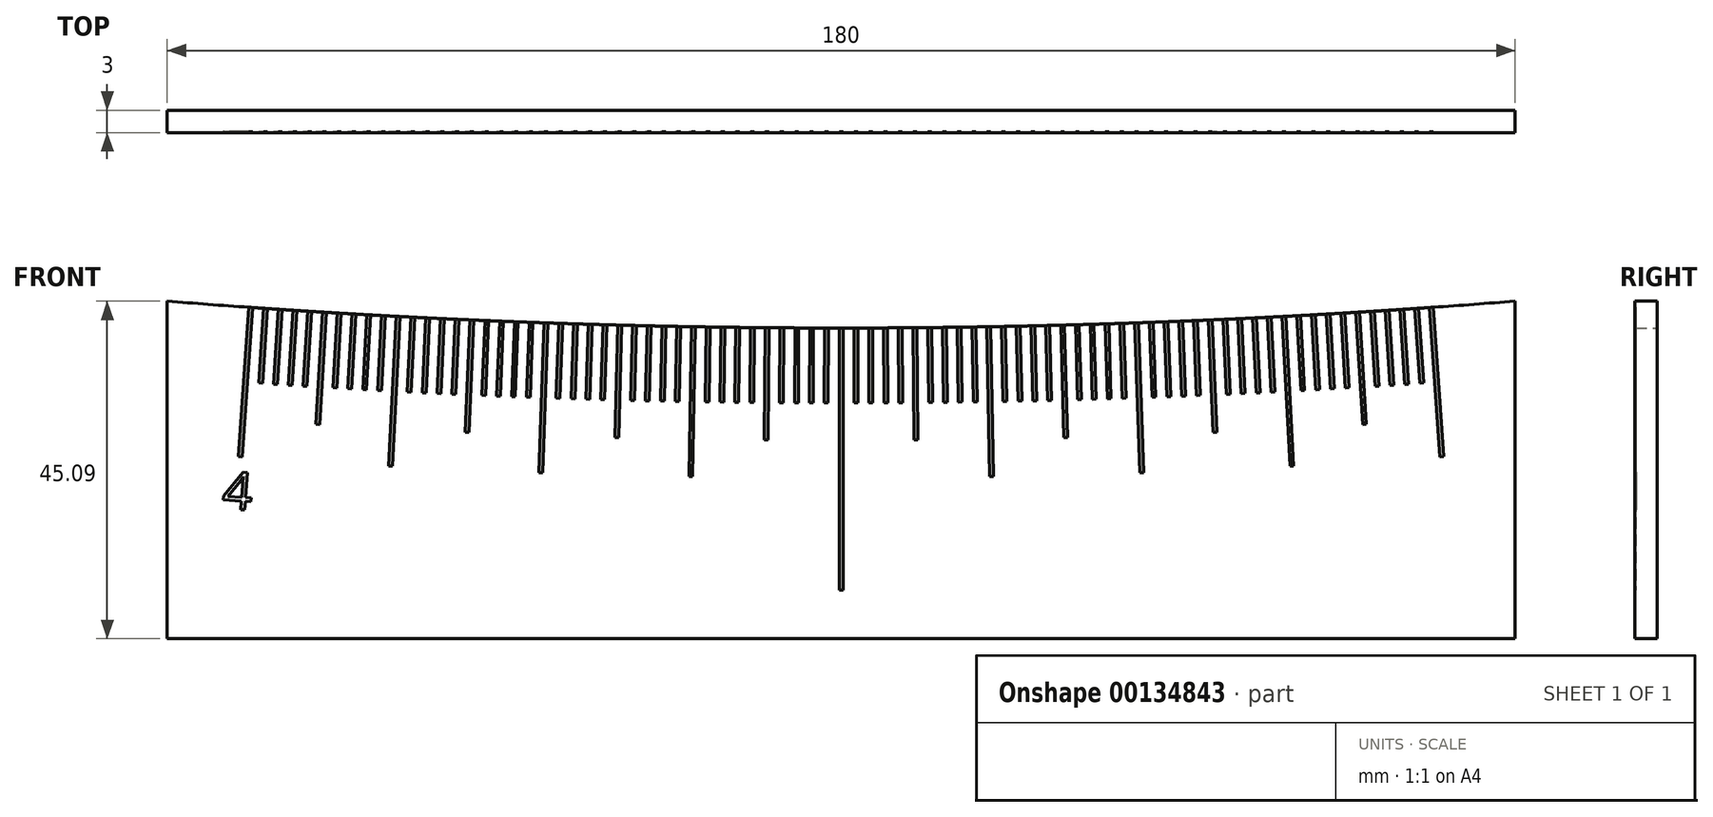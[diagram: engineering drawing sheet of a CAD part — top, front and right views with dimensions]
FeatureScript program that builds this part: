
annotation { "Feature Type Name" : "Feature", "Feature Type Description" : "" }
export const myFeature = defineFeature(function(context is Context, id is Id, definition is map)
    precondition{}
    {
        {
            var Q0;
            Q0=qCreatedBy(makeId("Front.planeOp"),FACE);
            var sketch = newSketch(context, id + "F0", { "sketchPlane" : qUnion([Q0])});
            skCircle(sketch, "E0", {"center": v(0, 1130) * mm, "radius": 1130 * mm});
            skLineSegment(sketch, "E1.rect.bottom", {"start": v(90, -41.5) * mm, "end": v(-90, -41.5) * mm});
            skLineSegment(sketch, "E1.rect.top", {"start": v(90, 41.5) * mm, "end": v(-90, 41.5) * mm});
            skLineSegment(sketch, "E1.rect.left", {"start": v(90, -41.5) * mm, "end": v(90, 41.5) * mm});
            skLineSegment(sketch, "E1.rect.right", {"start": v(-90, -41.5) * mm, "end": v(-90, 41.5) * mm});
            skPoint(sketch, "E1.rect.middle", {"position": v(0, 0) * mm});
            skSolve(sketch);
        }
        {
            var Q0;
            {var subQ3=sQuery(id+"F0.wireOp",EDGE,"E1.rect.bottom");Q0=makeQuery(id+"F0.imprint","IMPRINT",FACE,{"disambiguationData":[TD([[makeQuery(id+"F0.imprint","IMPRINT",EDGE,{"derivedFrom":subQ3}),-1.0]])]});}
            extrude(context, id + "F1", {"entities" : qUnion([Q0]), "depth" : 3 * mm});
        }
        {
            var Q0;
            Q0=makeQuery(id+"F1.opExtrude","CAP_FACE",FACE,{"disambiguationData":[OSD([sQuery(id+"F0.wireOp",EDGE,"E0"),sQuery(id+"F0.wireOp",EDGE,"E1.rect.bottom"),sQuery(id+"F0.wireOp",EDGE,"E1.rect.left"),sQuery(id+"F0.wireOp",EDGE,"E1.rect.right")])],"isStart":false});
            var sketch = newSketch(context, id + "F2", { "sketchPlane" : qUnion([Q0])});
            skLineSegment(sketch, "E2.rect.bottom", {"start": v(0.25, 20) * mm, "end": v(-0.25, 20) * mm});
            skLineSegment(sketch, "E2.rect.top", {"start": v(0.25, -20) * mm, "end": v(-0.25, -20) * mm});
            skLineSegment(sketch, "E2.rect.left", {"start": v(0.25, 20) * mm, "end": v(0.25, -20) * mm});
            skLineSegment(sketch, "E2.rect.right", {"start": v(-0.25, 20) * mm, "end": v(-0.25, -20) * mm});
            skPoint(sketch, "E2.rect.middle", {"position": v(0, 0) * mm});
            skLineSegment(sketch, "E3.1.0", {"start": v(-19.12, 20.16) * mm, "end": v(-19.62, 20.17) * mm});
            skLineSegment(sketch, "E3.1.1", {"start": v(-19.62, 20.17) * mm, "end": v(-20.32, -19.82) * mm});
            skLineSegment(sketch, "E3.1.2", {"start": v(-19.12, 20.16) * mm, "end": v(-19.82, -19.83) * mm});
            skLineSegment(sketch, "E3.1.3", {"start": v(-19.82, -19.83) * mm, "end": v(-20.32, -19.82) * mm});
            skLineSegment(sketch, "E3.2.0", {"start": v(-38.49, 20.67) * mm, "end": v(-38.99, 20.68) * mm});
            skLineSegment(sketch, "E3.2.1", {"start": v(-38.99, 20.68) * mm, "end": v(-40.38, -19.3) * mm});
            skLineSegment(sketch, "E3.2.2", {"start": v(-38.49, 20.67) * mm, "end": v(-39.88, -19.3) * mm});
            skLineSegment(sketch, "E3.2.3", {"start": v(-39.88, -19.3) * mm, "end": v(-40.38, -19.3) * mm});
            skLineSegment(sketch, "E3.3.0", {"start": v(-57.84, 21.5) * mm, "end": v(-58.34, 21.53) * mm});
            skLineSegment(sketch, "E3.3.1", {"start": v(-58.34, 21.53) * mm, "end": v(-60.44, -18.41) * mm});
            skLineSegment(sketch, "E3.3.2", {"start": v(-57.84, 21.5) * mm, "end": v(-59.94, -18.44) * mm});
            skLineSegment(sketch, "E3.3.3", {"start": v(-59.94, -18.44) * mm, "end": v(-60.44, -18.41) * mm});
            skLineSegment(sketch, "E3.4.0", {"start": v(-77.18, 22.69) * mm, "end": v(-77.68, 22.72) * mm});
            skLineSegment(sketch, "E3.4.1", {"start": v(-77.68, 22.72) * mm, "end": v(-80.47, -17.18) * mm});
            skLineSegment(sketch, "E3.4.2", {"start": v(-77.18, 22.69) * mm, "end": v(-79.97, -17.22) * mm});
            skLineSegment(sketch, "E3.4.3", {"start": v(-79.97, -17.22) * mm, "end": v(-80.47, -17.18) * mm});
            skPoint(sketch, "E3.center", {"position": v(0, 1130) * mm});
            skLineSegment(sketch, "E3.anchor1", {"start": v(0, 1130) * mm, "end": v(-0.25, 20) * mm, "construction": true});
            skLineSegment(sketch, "E3.anchor2", {"start": v(0, 1130) * mm, "end": v(-77.68, 22.72) * mm, "construction": true});
            skSolve(sketch);
        }
        {
            var Q0;
            Q0=qSketchRegion(id+"F2",true);
            extrude(context, id + "F3", {"entities" : qUnion([Q0]), "operationType" : NewBodyOperationType.REMOVE, "oppositeDirection" : true, "depth" : 0.1 * mm});
        }
        {
            var Q0;
            Q0=makeQuery(id+"F1.opExtrude","SWEPT_BODY",BODY,{"disambiguationData":[OSD([sQuery(id+"F0.wireOp",EDGE,"E0"),sQuery(id+"F0.wireOp",EDGE,"E1.rect.bottom"),sQuery(id+"F0.wireOp",EDGE,"E1.rect.left"),sQuery(id+"F0.wireOp",EDGE,"E1.rect.right")])]});
            var Q1;
            Q1=qCreatedBy(makeId("Right.planeOp"),FACE);
            mirror(context, id + "F4", {"operationType" : NewBodyOperationType.INTERSECT, "entities" : qUnion([Q0]), "mirrorPlane" : qUnion([Q1])});
        }
        {
            var Q0;
            Q0=makeQuery(id+"F1.opExtrude","CAP_FACE",FACE,{"disambiguationData":[OSD([sQuery(id+"F0.wireOp",EDGE,"E0"),sQuery(id+"F0.wireOp",EDGE,"E1.rect.bottom"),sQuery(id+"F0.wireOp",EDGE,"E1.rect.left"),sQuery(id+"F0.wireOp",EDGE,"E1.rect.right")])],"isStart":false});
            var sketch = newSketch(context, id + "F5", { "sketchPlane" : qUnion([Q0])});
            skLineSegment(sketch, "E4.rect.bottom", {"start": v(0.25, 10) * mm, "end": v(-0.25, 10) * mm});
            skLineSegment(sketch, "E4.rect.top", {"start": v(0.25, -10) * mm, "end": v(-0.25, -10) * mm});
            skLineSegment(sketch, "E4.rect.left", {"start": v(0.25, 10) * mm, "end": v(0.25, -10) * mm});
            skLineSegment(sketch, "E4.rect.right", {"start": v(-0.25, 10) * mm, "end": v(-0.25, -10) * mm});
            skPoint(sketch, "E4.rect.middle", {"position": v(0, 0) * mm});
            skLineSegment(sketch, "E5.1.0", {"start": v(-1.74, -10) * mm, "end": v(-2.24, -10) * mm});
            skLineSegment(sketch, "E5.1.1", {"start": v(-1.7, 10) * mm, "end": v(-1.74, -10) * mm});
            skLineSegment(sketch, "E5.1.2", {"start": v(-2.2, 10) * mm, "end": v(-2.24, -10) * mm});
            skLineSegment(sketch, "E5.1.3", {"start": v(-1.7, 10) * mm, "end": v(-2.2, 10) * mm});
            skLineSegment(sketch, "E5.2.0", {"start": v(-3.73, -10) * mm, "end": v(-4.23, -10) * mm});
            skLineSegment(sketch, "E5.2.1", {"start": v(-3.66, 10) * mm, "end": v(-3.73, -10) * mm});
            skLineSegment(sketch, "E5.2.2", {"start": v(-4.16, 10) * mm, "end": v(-4.23, -10) * mm});
            skLineSegment(sketch, "E5.2.3", {"start": v(-3.66, 10) * mm, "end": v(-4.16, 10) * mm});
            skLineSegment(sketch, "E5.3.0", {"start": v(-5.72, -9.99) * mm, "end": v(-6.22, -9.98) * mm});
            skLineSegment(sketch, "E5.3.1", {"start": v(-5.61, 10.01) * mm, "end": v(-5.72, -9.99) * mm});
            skLineSegment(sketch, "E5.3.2", {"start": v(-6.11, 10.02) * mm, "end": v(-6.22, -9.98) * mm});
            skLineSegment(sketch, "E5.3.3", {"start": v(-5.61, 10.01) * mm, "end": v(-6.11, 10.02) * mm});
            skLineSegment(sketch, "E5.4.0", {"start": v(-7.7, -9.97) * mm, "end": v(-8.2, -9.97) * mm});
            skLineSegment(sketch, "E5.4.1", {"start": v(-7.57, 10.03) * mm, "end": v(-7.7, -9.97) * mm});
            skLineSegment(sketch, "E5.4.2", {"start": v(-8.07, 10.03) * mm, "end": v(-8.2, -9.97) * mm});
            skLineSegment(sketch, "E5.4.3", {"start": v(-7.57, 10.03) * mm, "end": v(-8.07, 10.03) * mm});
            skLineSegment(sketch, "E5.5.0", {"start": v(-9.7, -9.96) * mm, "end": v(-10.2, -9.95) * mm});
            skLineSegment(sketch, "E5.5.1", {"start": v(-9.52, 10.04) * mm, "end": v(-9.7, -9.96) * mm});
            skLineSegment(sketch, "E5.5.2", {"start": v(-10.02, 10.04) * mm, "end": v(-10.2, -9.95) * mm});
            skLineSegment(sketch, "E5.5.3", {"start": v(-9.52, 10.04) * mm, "end": v(-10.02, 10.04) * mm});
            skLineSegment(sketch, "E5.6.0", {"start": v(-11.69, -9.94) * mm, "end": v(-12.19, -9.93) * mm});
            skLineSegment(sketch, "E5.6.1", {"start": v(-11.48, 10.06) * mm, "end": v(-11.69, -9.94) * mm});
            skLineSegment(sketch, "E5.6.2", {"start": v(-11.98, 10.06) * mm, "end": v(-12.19, -9.93) * mm});
            skLineSegment(sketch, "E5.6.3", {"start": v(-11.48, 10.06) * mm, "end": v(-11.98, 10.06) * mm});
            skLineSegment(sketch, "E5.7.0", {"start": v(-13.68, -9.92) * mm, "end": v(-14.18, -9.91) * mm});
            skLineSegment(sketch, "E5.7.1", {"start": v(-13.43, 10.08) * mm, "end": v(-13.68, -9.92) * mm});
            skLineSegment(sketch, "E5.7.2", {"start": v(-13.93, 10.09) * mm, "end": v(-14.18, -9.91) * mm});
            skLineSegment(sketch, "E5.7.3", {"start": v(-13.43, 10.08) * mm, "end": v(-13.93, 10.09) * mm});
            skLineSegment(sketch, "E5.8.0", {"start": v(-15.67, -9.9) * mm, "end": v(-16.17, -9.89) * mm});
            skLineSegment(sketch, "E5.8.1", {"start": v(-15.39, 10.1) * mm, "end": v(-15.67, -9.9) * mm});
            skLineSegment(sketch, "E5.8.2", {"start": v(-15.89, 10.11) * mm, "end": v(-16.17, -9.89) * mm});
            skLineSegment(sketch, "E5.8.3", {"start": v(-15.39, 10.1) * mm, "end": v(-15.89, 10.11) * mm});
            skLineSegment(sketch, "E5.9.0", {"start": v(-17.66, -9.86) * mm, "end": v(-18.16, -9.86) * mm});
            skLineSegment(sketch, "E5.9.1", {"start": v(-17.34, 10.13) * mm, "end": v(-17.66, -9.86) * mm});
            skLineSegment(sketch, "E5.9.2", {"start": v(-17.84, 10.14) * mm, "end": v(-18.16, -9.86) * mm});
            skLineSegment(sketch, "E5.9.3", {"start": v(-17.34, 10.13) * mm, "end": v(-17.84, 10.14) * mm});
            skLineSegment(sketch, "E5.10.0", {"start": v(-19.65, -9.83) * mm, "end": v(-20.15, -9.82) * mm});
            skLineSegment(sketch, "E5.10.1", {"start": v(-19.3, 10.17) * mm, "end": v(-19.65, -9.83) * mm});
            skLineSegment(sketch, "E5.10.2", {"start": v(-19.8, 10.17) * mm, "end": v(-20.15, -9.82) * mm});
            skLineSegment(sketch, "E5.10.3", {"start": v(-19.3, 10.17) * mm, "end": v(-19.8, 10.17) * mm});
            skLineSegment(sketch, "E5.11.0", {"start": v(-21.64, -9.8) * mm, "end": v(-22.14, -9.79) * mm});
            skLineSegment(sketch, "E5.11.1", {"start": v(-21.25, 10.2) * mm, "end": v(-21.64, -9.8) * mm});
            skLineSegment(sketch, "E5.11.2", {"start": v(-21.75, 10.21) * mm, "end": v(-22.14, -9.79) * mm});
            skLineSegment(sketch, "E5.11.3", {"start": v(-21.25, 10.2) * mm, "end": v(-21.75, 10.21) * mm});
            skLineSegment(sketch, "E5.12.0", {"start": v(-23.62, -9.76) * mm, "end": v(-24.12, -9.74) * mm});
            skLineSegment(sketch, "E5.12.1", {"start": v(-23.2, 10.24) * mm, "end": v(-23.62, -9.76) * mm});
            skLineSegment(sketch, "E5.12.2", {"start": v(-23.7, 10.25) * mm, "end": v(-24.12, -9.74) * mm});
            skLineSegment(sketch, "E5.12.3", {"start": v(-23.2, 10.24) * mm, "end": v(-23.7, 10.25) * mm});
            skLineSegment(sketch, "E5.13.0", {"start": v(-25.61, -9.71) * mm, "end": v(-26.11, -9.7) * mm});
            skLineSegment(sketch, "E5.13.1", {"start": v(-25.16, 10.28) * mm, "end": v(-25.61, -9.71) * mm});
            skLineSegment(sketch, "E5.13.2", {"start": v(-25.66, 10.3) * mm, "end": v(-26.11, -9.7) * mm});
            skLineSegment(sketch, "E5.13.3", {"start": v(-25.16, 10.28) * mm, "end": v(-25.66, 10.3) * mm});
            skLineSegment(sketch, "E5.14.0", {"start": v(-27.6, -9.67) * mm, "end": v(-28.1, -9.65) * mm});
            skLineSegment(sketch, "E5.14.1", {"start": v(-27.11, 10.33) * mm, "end": v(-27.6, -9.67) * mm});
            skLineSegment(sketch, "E5.14.2", {"start": v(-27.61, 10.34) * mm, "end": v(-28.1, -9.65) * mm});
            skLineSegment(sketch, "E5.14.3", {"start": v(-27.11, 10.33) * mm, "end": v(-27.61, 10.34) * mm});
            skLineSegment(sketch, "E5.15.0", {"start": v(-29.6, -9.62) * mm, "end": v(-30.1, -9.6) * mm});
            skLineSegment(sketch, "E5.15.1", {"start": v(-29.07, 10.38) * mm, "end": v(-29.6, -9.62) * mm});
            skLineSegment(sketch, "E5.15.2", {"start": v(-29.57, 10.4) * mm, "end": v(-30.1, -9.6) * mm});
            skLineSegment(sketch, "E5.15.3", {"start": v(-29.07, 10.38) * mm, "end": v(-29.57, 10.4) * mm});
            skLineSegment(sketch, "E5.16.0", {"start": v(-31.58, -9.56) * mm, "end": v(-32.08, -9.55) * mm});
            skLineSegment(sketch, "E5.16.1", {"start": v(-31.02, 10.43) * mm, "end": v(-31.58, -9.56) * mm});
            skLineSegment(sketch, "E5.16.2", {"start": v(-31.52, 10.44) * mm, "end": v(-32.08, -9.55) * mm});
            skLineSegment(sketch, "E5.16.3", {"start": v(-31.02, 10.43) * mm, "end": v(-31.52, 10.44) * mm});
            skLineSegment(sketch, "E5.17.0", {"start": v(-33.57, -9.5) * mm, "end": v(-34.07, -9.5) * mm});
            skLineSegment(sketch, "E5.17.1", {"start": v(-32.98, 10.49) * mm, "end": v(-33.57, -9.5) * mm});
            skLineSegment(sketch, "E5.17.2", {"start": v(-33.48, 10.5) * mm, "end": v(-34.07, -9.5) * mm});
            skLineSegment(sketch, "E5.17.3", {"start": v(-32.98, 10.49) * mm, "end": v(-33.48, 10.5) * mm});
            skLineSegment(sketch, "E5.18.0", {"start": v(-35.56, -9.45) * mm, "end": v(-36.06, -9.43) * mm});
            skLineSegment(sketch, "E5.18.1", {"start": v(-34.93, 10.54) * mm, "end": v(-35.56, -9.45) * mm});
            skLineSegment(sketch, "E5.18.2", {"start": v(-35.43, 10.56) * mm, "end": v(-36.06, -9.43) * mm});
            skLineSegment(sketch, "E5.18.3", {"start": v(-34.93, 10.54) * mm, "end": v(-35.43, 10.56) * mm});
            skLineSegment(sketch, "E5.19.0", {"start": v(-37.55, -9.38) * mm, "end": v(-38.05, -9.36) * mm});
            skLineSegment(sketch, "E5.19.1", {"start": v(-36.88, 10.6) * mm, "end": v(-37.55, -9.38) * mm});
            skLineSegment(sketch, "E5.19.2", {"start": v(-37.38, 10.62) * mm, "end": v(-38.05, -9.36) * mm});
            skLineSegment(sketch, "E5.19.3", {"start": v(-36.88, 10.6) * mm, "end": v(-37.38, 10.62) * mm});
            skLineSegment(sketch, "E5.20.0", {"start": v(-39.54, -9.31) * mm, "end": v(-40.04, -9.3) * mm});
            skLineSegment(sketch, "E5.20.1", {"start": v(-38.84, 10.67) * mm, "end": v(-39.54, -9.31) * mm});
            skLineSegment(sketch, "E5.20.2", {"start": v(-39.34, 10.7) * mm, "end": v(-40.04, -9.3) * mm});
            skLineSegment(sketch, "E5.20.3", {"start": v(-38.84, 10.67) * mm, "end": v(-39.34, 10.7) * mm});
            skLineSegment(sketch, "E5.21.0", {"start": v(-41.52, -9.24) * mm, "end": v(-42.02, -9.23) * mm});
            skLineSegment(sketch, "E5.21.1", {"start": v(-40.8, 10.74) * mm, "end": v(-41.52, -9.24) * mm});
            skLineSegment(sketch, "E5.21.2", {"start": v(-41.3, 10.76) * mm, "end": v(-42.02, -9.23) * mm});
            skLineSegment(sketch, "E5.21.3", {"start": v(-40.8, 10.74) * mm, "end": v(-41.3, 10.76) * mm});
            skLineSegment(sketch, "E5.22.0", {"start": v(-43.51, -9.17) * mm, "end": v(-44.01, -9.15) * mm});
            skLineSegment(sketch, "E5.22.1", {"start": v(-42.74, 10.82) * mm, "end": v(-43.51, -9.17) * mm});
            skLineSegment(sketch, "E5.22.2", {"start": v(-43.24, 10.84) * mm, "end": v(-44.01, -9.15) * mm});
            skLineSegment(sketch, "E5.22.3", {"start": v(-42.74, 10.82) * mm, "end": v(-43.24, 10.84) * mm});
            skLineSegment(sketch, "E5.23.0", {"start": v(-45.5, -9.1) * mm, "end": v(-46, -9.07) * mm});
            skLineSegment(sketch, "E5.23.1", {"start": v(-44.7, 10.9) * mm, "end": v(-45.5, -9.1) * mm});
            skLineSegment(sketch, "E5.23.2", {"start": v(-45.2, 10.91) * mm, "end": v(-46, -9.07) * mm});
            skLineSegment(sketch, "E5.23.3", {"start": v(-44.7, 10.9) * mm, "end": v(-45.2, 10.91) * mm});
            skLineSegment(sketch, "E5.24.0", {"start": v(-47.49, -9.01) * mm, "end": v(-47.99, -8.99) * mm});
            skLineSegment(sketch, "E5.24.1", {"start": v(-46.65, 10.97) * mm, "end": v(-47.49, -9.01) * mm});
            skLineSegment(sketch, "E5.24.2", {"start": v(-47.15, 11) * mm, "end": v(-47.99, -8.99) * mm});
            skLineSegment(sketch, "E5.24.3", {"start": v(-46.65, 10.97) * mm, "end": v(-47.15, 11) * mm});
            skLineSegment(sketch, "E5.25.0", {"start": v(-49.48, -8.93) * mm, "end": v(-49.98, -8.9) * mm});
            skLineSegment(sketch, "E5.25.1", {"start": v(-48.6, 11.06) * mm, "end": v(-49.48, -8.93) * mm});
            skLineSegment(sketch, "E5.25.2", {"start": v(-49.1, 11.08) * mm, "end": v(-49.98, -8.9) * mm});
            skLineSegment(sketch, "E5.25.3", {"start": v(-48.6, 11.06) * mm, "end": v(-49.1, 11.08) * mm});
            skLineSegment(sketch, "E5.26.0", {"start": v(-51.46, -8.84) * mm, "end": v(-51.96, -8.82) * mm});
            skLineSegment(sketch, "E5.26.1", {"start": v(-50.56, 11.14) * mm, "end": v(-51.46, -8.84) * mm});
            skLineSegment(sketch, "E5.26.2", {"start": v(-51.06, 11.16) * mm, "end": v(-51.96, -8.82) * mm});
            skLineSegment(sketch, "E5.26.3", {"start": v(-50.56, 11.14) * mm, "end": v(-51.06, 11.16) * mm});
            skLineSegment(sketch, "E5.27.0", {"start": v(-53.45, -8.75) * mm, "end": v(-53.95, -8.72) * mm});
            skLineSegment(sketch, "E5.27.1", {"start": v(-52.5, 11.23) * mm, "end": v(-53.45, -8.75) * mm});
            skLineSegment(sketch, "E5.27.2", {"start": v(-53, 11.26) * mm, "end": v(-53.95, -8.72) * mm});
            skLineSegment(sketch, "E5.27.3", {"start": v(-52.5, 11.23) * mm, "end": v(-53, 11.26) * mm});
            skLineSegment(sketch, "E5.28.0", {"start": v(-55.44, -8.65) * mm, "end": v(-55.94, -8.63) * mm});
            skLineSegment(sketch, "E5.28.1", {"start": v(-54.46, 11.32) * mm, "end": v(-55.44, -8.65) * mm});
            skLineSegment(sketch, "E5.28.2", {"start": v(-54.96, 11.35) * mm, "end": v(-55.94, -8.63) * mm});
            skLineSegment(sketch, "E5.28.3", {"start": v(-54.46, 11.32) * mm, "end": v(-54.96, 11.35) * mm});
            skLineSegment(sketch, "E5.29.0", {"start": v(-57.43, -8.55) * mm, "end": v(-57.93, -8.53) * mm});
            skLineSegment(sketch, "E5.29.1", {"start": v(-56.41, 11.42) * mm, "end": v(-57.43, -8.55) * mm});
            skLineSegment(sketch, "E5.29.2", {"start": v(-56.91, 11.45) * mm, "end": v(-57.93, -8.53) * mm});
            skLineSegment(sketch, "E5.29.3", {"start": v(-56.41, 11.42) * mm, "end": v(-56.91, 11.45) * mm});
            skLineSegment(sketch, "E5.30.0", {"start": v(-59.41, -8.45) * mm, "end": v(-59.91, -8.42) * mm});
            skLineSegment(sketch, "E5.30.1", {"start": v(-58.37, 11.52) * mm, "end": v(-59.41, -8.45) * mm});
            skLineSegment(sketch, "E5.30.2", {"start": v(-58.87, 11.55) * mm, "end": v(-59.91, -8.42) * mm});
            skLineSegment(sketch, "E5.30.3", {"start": v(-58.37, 11.52) * mm, "end": v(-58.87, 11.55) * mm});
            skLineSegment(sketch, "E5.31.0", {"start": v(-61.4, -8.35) * mm, "end": v(-61.9, -8.32) * mm});
            skLineSegment(sketch, "E5.31.1", {"start": v(-60.32, 11.63) * mm, "end": v(-61.4, -8.35) * mm});
            skLineSegment(sketch, "E5.31.2", {"start": v(-60.82, 11.65) * mm, "end": v(-61.9, -8.32) * mm});
            skLineSegment(sketch, "E5.31.3", {"start": v(-60.32, 11.63) * mm, "end": v(-60.82, 11.65) * mm});
            skLineSegment(sketch, "E5.32.0", {"start": v(-63.39, -8.24) * mm, "end": v(-63.89, -8.2) * mm});
            skLineSegment(sketch, "E5.32.1", {"start": v(-62.27, 11.73) * mm, "end": v(-63.39, -8.24) * mm});
            skLineSegment(sketch, "E5.32.2", {"start": v(-62.77, 11.76) * mm, "end": v(-63.89, -8.2) * mm});
            skLineSegment(sketch, "E5.32.3", {"start": v(-62.27, 11.73) * mm, "end": v(-62.77, 11.76) * mm});
            skLineSegment(sketch, "E5.33.0", {"start": v(-65.37, -8.12) * mm, "end": v(-65.87, -8.1) * mm});
            skLineSegment(sketch, "E5.33.1", {"start": v(-64.22, 11.84) * mm, "end": v(-65.37, -8.12) * mm});
            skLineSegment(sketch, "E5.33.2", {"start": v(-64.72, 11.87) * mm, "end": v(-65.87, -8.1) * mm});
            skLineSegment(sketch, "E5.33.3", {"start": v(-64.22, 11.84) * mm, "end": v(-64.72, 11.87) * mm});
            skLineSegment(sketch, "E5.34.0", {"start": v(-67.36, -8) * mm, "end": v(-67.86, -7.98) * mm});
            skLineSegment(sketch, "E5.34.1", {"start": v(-66.17, 11.96) * mm, "end": v(-67.36, -8) * mm});
            skLineSegment(sketch, "E5.34.2", {"start": v(-66.67, 11.99) * mm, "end": v(-67.86, -7.98) * mm});
            skLineSegment(sketch, "E5.34.3", {"start": v(-66.17, 11.96) * mm, "end": v(-66.67, 11.99) * mm});
            skLineSegment(sketch, "E5.35.0", {"start": v(-69.35, -7.89) * mm, "end": v(-69.84, -7.86) * mm});
            skLineSegment(sketch, "E5.35.1", {"start": v(-68.12, 12.07) * mm, "end": v(-69.35, -7.89) * mm});
            skLineSegment(sketch, "E5.35.2", {"start": v(-68.62, 12.1) * mm, "end": v(-69.84, -7.86) * mm});
            skLineSegment(sketch, "E5.35.3", {"start": v(-68.12, 12.07) * mm, "end": v(-68.62, 12.1) * mm});
            skLineSegment(sketch, "E5.36.0", {"start": v(-71.33, -7.77) * mm, "end": v(-71.83, -7.73) * mm});
            skLineSegment(sketch, "E5.36.1", {"start": v(-70.08, 12.2) * mm, "end": v(-71.33, -7.77) * mm});
            skLineSegment(sketch, "E5.36.2", {"start": v(-70.57, 12.23) * mm, "end": v(-71.83, -7.73) * mm});
            skLineSegment(sketch, "E5.36.3", {"start": v(-70.08, 12.2) * mm, "end": v(-70.57, 12.23) * mm});
            skLineSegment(sketch, "E5.37.0", {"start": v(-73.32, -7.64) * mm, "end": v(-73.82, -7.6) * mm});
            skLineSegment(sketch, "E5.37.1", {"start": v(-72.03, 12.32) * mm, "end": v(-73.32, -7.64) * mm});
            skLineSegment(sketch, "E5.37.2", {"start": v(-72.53, 12.35) * mm, "end": v(-73.82, -7.6) * mm});
            skLineSegment(sketch, "E5.37.3", {"start": v(-72.03, 12.32) * mm, "end": v(-72.53, 12.35) * mm});
            skLineSegment(sketch, "E5.38.0", {"start": v(-75.3, -7.51) * mm, "end": v(-75.8, -7.48) * mm});
            skLineSegment(sketch, "E5.38.1", {"start": v(-73.98, 12.45) * mm, "end": v(-75.3, -7.51) * mm});
            skLineSegment(sketch, "E5.38.2", {"start": v(-74.48, 12.48) * mm, "end": v(-75.8, -7.48) * mm});
            skLineSegment(sketch, "E5.38.3", {"start": v(-73.98, 12.45) * mm, "end": v(-74.48, 12.48) * mm});
            skLineSegment(sketch, "E5.39.0", {"start": v(-77.29, -7.38) * mm, "end": v(-77.79, -7.34) * mm});
            skLineSegment(sketch, "E5.39.1", {"start": v(-75.93, 12.58) * mm, "end": v(-77.29, -7.38) * mm});
            skLineSegment(sketch, "E5.39.2", {"start": v(-76.43, 12.61) * mm, "end": v(-77.79, -7.34) * mm});
            skLineSegment(sketch, "E5.39.3", {"start": v(-75.93, 12.58) * mm, "end": v(-76.43, 12.61) * mm});
            skPoint(sketch, "E5.center", {"position": v(0, 1130) * mm});
            skLineSegment(sketch, "E5.anchor1", {"start": v(0, 1130) * mm, "end": v(-0.25, -10) * mm, "construction": true});
            skLineSegment(sketch, "E5.anchor2", {"start": v(0, 1130) * mm, "end": v(-79.77, -7.2) * mm, "construction": true});
            skLineSegment(sketch, "E6.2.40.0", {"start": v(-79.27, -7.24) * mm, "end": v(-79.77, -7.2) * mm});
            skLineSegment(sketch, "E6.3.40.0", {"start": v(-77.88, 12.71) * mm, "end": v(-79.27, -7.24) * mm});
            skLineSegment(sketch, "E6.6.40.0", {"start": v(-78.38, 12.75) * mm, "end": v(-79.77, -7.2) * mm});
            skLineSegment(sketch, "E6.9.40.0", {"start": v(-77.88, 12.71) * mm, "end": v(-78.38, 12.75) * mm});
            skSolve(sketch);
        }
        {
            var Q0;
            Q0=qSketchRegion(id+"F5",true);
            extrude(context, id + "F6", {"entities" : qUnion([Q0]), "operationType" : NewBodyOperationType.REMOVE, "oppositeDirection" : true, "depth" : 0.1 * mm});
        }
        {
            var Q0;
            Q0=makeQuery(id+"F1.opExtrude","SWEPT_BODY",BODY,{"disambiguationData":[OSD([sQuery(id+"F0.wireOp",EDGE,"E0"),sQuery(id+"F0.wireOp",EDGE,"E1.rect.bottom"),sQuery(id+"F0.wireOp",EDGE,"E1.rect.left"),sQuery(id+"F0.wireOp",EDGE,"E1.rect.right")])]});
            var Q1;
            Q1=qCreatedBy(makeId("Right.planeOp"),FACE);
            mirror(context, id + "F7", {"operationType" : NewBodyOperationType.INTERSECT, "entities" : qUnion([Q0]), "mirrorPlane" : qUnion([Q1])});
        }
        {
            var Q0;
            Q0=makeQuery(id+"F1.opExtrude","CAP_FACE",FACE,{"disambiguationData":[OSD([sQuery(id+"F0.wireOp",EDGE,"E0"),sQuery(id+"F0.wireOp",EDGE,"E1.rect.bottom"),sQuery(id+"F0.wireOp",EDGE,"E1.rect.left"),sQuery(id+"F0.wireOp",EDGE,"E1.rect.right")])],"isStart":false});
            var sketch = newSketch(context, id + "F8", { "sketchPlane" : qUnion([Q0])});
            skLineSegment(sketch, "E7.rect.bottom", {"start": v(-0.25, -35) * mm, "end": v(0.25, -35) * mm});
            skLineSegment(sketch, "E7.rect.top", {"start": v(-0.25, 35) * mm, "end": v(0.25, 35) * mm});
            skLineSegment(sketch, "E7.rect.left", {"start": v(-0.25, -35) * mm, "end": v(-0.25, 35) * mm});
            skLineSegment(sketch, "E7.rect.right", {"start": v(0.25, -35) * mm, "end": v(0.25, 35) * mm});
            skPoint(sketch, "E7.rect.middle", {"position": v(0, 0) * mm});
            skSolve(sketch);
        }
        {
            var Q0;
            Q0=qSketchRegion(id+"F8",true);
            extrude(context, id + "F9", {"entities" : qUnion([Q0]), "operationType" : NewBodyOperationType.REMOVE, "oppositeDirection" : true, "depth" : 0.1 * mm});
        }
        {
            var Q0;
            Q0=makeQuery(id+"F1.opExtrude","CAP_FACE",FACE,{"disambiguationData":[OSD([sQuery(id+"F0.wireOp",EDGE,"E0"),sQuery(id+"F0.wireOp",EDGE,"E1.rect.bottom"),sQuery(id+"F0.wireOp",EDGE,"E1.rect.left"),sQuery(id+"F0.wireOp",EDGE,"E1.rect.right")])],"isStart":false});
            var sketch = newSketch(context, id + "F10", { "sketchPlane" : qUnion([Q0])});
            skLineSegment(sketch, "E8.rect.bottom", {"start": v(-0.25, -15) * mm, "end": v(0.25, -15) * mm});
            skLineSegment(sketch, "E8.rect.top", {"start": v(-0.25, 15) * mm, "end": v(0.25, 15) * mm});
            skLineSegment(sketch, "E8.rect.left", {"start": v(-0.25, -15) * mm, "end": v(-0.25, 15) * mm});
            skLineSegment(sketch, "E8.rect.right", {"start": v(0.25, -15) * mm, "end": v(0.25, 15) * mm});
            skPoint(sketch, "E8.rect.middle", {"position": v(0, 0) * mm});
            skLineSegment(sketch, "E9.1.0", {"start": v(-10.24, -14.95) * mm, "end": v(-9.74, -14.96) * mm});
            skLineSegment(sketch, "E9.1.1", {"start": v(-9.74, -14.96) * mm, "end": v(-9.48, 15.04) * mm});
            skLineSegment(sketch, "E9.1.2", {"start": v(-10.24, -14.95) * mm, "end": v(-9.98, 15.04) * mm});
            skLineSegment(sketch, "E9.1.3", {"start": v(-9.98, 15.04) * mm, "end": v(-9.48, 15.04) * mm});
            skLineSegment(sketch, "E9.2.0", {"start": v(-20.23, -14.82) * mm, "end": v(-19.73, -14.83) * mm});
            skLineSegment(sketch, "E9.2.1", {"start": v(-19.73, -14.83) * mm, "end": v(-19.2, 15.17) * mm});
            skLineSegment(sketch, "E9.2.2", {"start": v(-20.23, -14.82) * mm, "end": v(-19.7, 15.17) * mm});
            skLineSegment(sketch, "E9.2.3", {"start": v(-19.7, 15.17) * mm, "end": v(-19.2, 15.17) * mm});
            skLineSegment(sketch, "E9.3.0", {"start": v(-30.22, -14.6) * mm, "end": v(-29.72, -14.61) * mm});
            skLineSegment(sketch, "E9.3.1", {"start": v(-29.72, -14.61) * mm, "end": v(-28.94, 15.38) * mm});
            skLineSegment(sketch, "E9.3.2", {"start": v(-30.22, -14.6) * mm, "end": v(-29.44, 15.39) * mm});
            skLineSegment(sketch, "E9.3.3", {"start": v(-29.44, 15.39) * mm, "end": v(-28.94, 15.38) * mm});
            skLineSegment(sketch, "E9.4.0", {"start": v(-40.2, -14.3) * mm, "end": v(-39.71, -14.31) * mm});
            skLineSegment(sketch, "E9.4.1", {"start": v(-39.71, -14.31) * mm, "end": v(-38.66, 15.67) * mm});
            skLineSegment(sketch, "E9.4.2", {"start": v(-40.2, -14.3) * mm, "end": v(-39.16, 15.69) * mm});
            skLineSegment(sketch, "E9.4.3", {"start": v(-39.16, 15.69) * mm, "end": v(-38.66, 15.67) * mm});
            skLineSegment(sketch, "E9.5.0", {"start": v(-50.2, -13.9) * mm, "end": v(-49.7, -13.92) * mm});
            skLineSegment(sketch, "E9.5.1", {"start": v(-49.7, -13.92) * mm, "end": v(-48.39, 16.05) * mm});
            skLineSegment(sketch, "E9.5.2", {"start": v(-50.2, -13.9) * mm, "end": v(-48.89, 16.07) * mm});
            skLineSegment(sketch, "E9.5.3", {"start": v(-48.89, 16.07) * mm, "end": v(-48.39, 16.05) * mm});
            skLineSegment(sketch, "E9.6.0", {"start": v(-60.17, -13.42) * mm, "end": v(-59.68, -13.44) * mm});
            skLineSegment(sketch, "E9.6.1", {"start": v(-59.68, -13.44) * mm, "end": v(-58.1, 16.51) * mm});
            skLineSegment(sketch, "E9.6.2", {"start": v(-60.17, -13.42) * mm, "end": v(-58.6, 16.54) * mm});
            skLineSegment(sketch, "E9.6.3", {"start": v(-58.6, 16.54) * mm, "end": v(-58.1, 16.51) * mm});
            skLineSegment(sketch, "E9.7.0", {"start": v(-70.15, -12.85) * mm, "end": v(-69.65, -12.88) * mm});
            skLineSegment(sketch, "E9.7.1", {"start": v(-69.65, -12.88) * mm, "end": v(-67.82, 17.06) * mm});
            skLineSegment(sketch, "E9.7.2", {"start": v(-70.15, -12.85) * mm, "end": v(-68.32, 17.1) * mm});
            skLineSegment(sketch, "E9.7.3", {"start": v(-68.32, 17.1) * mm, "end": v(-67.82, 17.06) * mm});
            skLineSegment(sketch, "E9.8.0", {"start": v(-80.12, -12.2) * mm, "end": v(-79.62, -12.23) * mm});
            skLineSegment(sketch, "E9.8.1", {"start": v(-79.62, -12.23) * mm, "end": v(-77.53, 17.7) * mm});
            skLineSegment(sketch, "E9.8.2", {"start": v(-80.12, -12.2) * mm, "end": v(-78.03, 17.73) * mm});
            skLineSegment(sketch, "E9.8.3", {"start": v(-78.03, 17.73) * mm, "end": v(-77.53, 17.7) * mm});
            skPoint(sketch, "E9.center", {"position": v(0, 1130) * mm});
            skLineSegment(sketch, "E9.anchor1", {"start": v(0, 1130) * mm, "end": v(-0.25, -15) * mm, "construction": true});
            skLineSegment(sketch, "E9.anchor2", {"start": v(0, 1130) * mm, "end": v(-80.12, -12.2) * mm, "construction": true});
            skSolve(sketch);
        }
        {
            var Q0;
            Q0=qSketchRegion(id+"F10",true);
            extrude(context, id + "F11", {"entities" : qUnion([Q0]), "operationType" : NewBodyOperationType.REMOVE, "oppositeDirection" : true, "depth" : 0.1 * mm});
        }
        {
            var Q0;
            Q0=makeQuery(id+"F1.opExtrude","SWEPT_BODY",BODY,{"disambiguationData":[OSD([sQuery(id+"F0.wireOp",EDGE,"E0"),sQuery(id+"F0.wireOp",EDGE,"E1.rect.bottom"),sQuery(id+"F0.wireOp",EDGE,"E1.rect.left"),sQuery(id+"F0.wireOp",EDGE,"E1.rect.right")])]});
            var Q1;
            Q1=qCreatedBy(makeId("Right.planeOp"),FACE);
            mirror(context, id + "F12", {"operationType" : NewBodyOperationType.INTERSECT, "entities" : qUnion([Q0]), "mirrorPlane" : qUnion([Q1])});
        }
        {
            var Q0;
            Q0=makeQuery(id+"F1.opExtrude","CAP_FACE",FACE,{"disambiguationData":[OSD([sQuery(id+"F0.wireOp",EDGE,"E0"),sQuery(id+"F0.wireOp",EDGE,"E1.rect.bottom"),sQuery(id+"F0.wireOp",EDGE,"E1.rect.left"),sQuery(id+"F0.wireOp",EDGE,"E1.rect.right")])],"isStart":false});
            var sketch = newSketch(context, id + "F13", { "sketchPlane" : qUnion([Q0])});
            skText(sketch, "E10", { "text": "4\n", "fontName": "OpenSans-Regular.ttf"});
            const initialGuessF13  = {"E10": [-0.08273, -0.02406, 0.99756, -0.06976, 0.005]};
            skSetInitialGuess(sketch, initialGuessF13);
            skSolve(sketch);
        }
        {
            var Q0;
            Q0=qSketchRegion(id+"F13",true);
            extrude(context, id + "F14", {"entities" : qUnion([Q0]), "operationType" : NewBodyOperationType.REMOVE, "oppositeDirection" : true, "depth" : 0.2 * mm});
        }
    });
